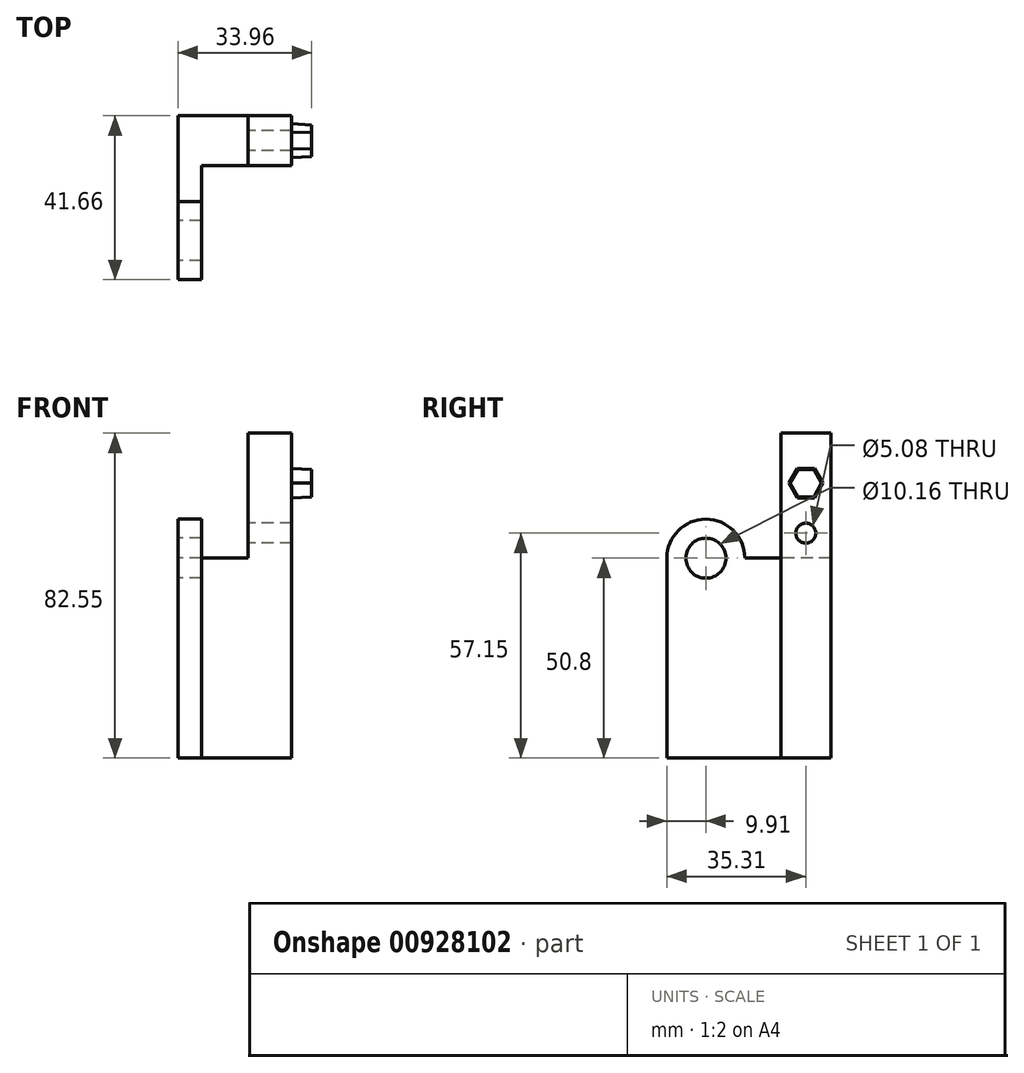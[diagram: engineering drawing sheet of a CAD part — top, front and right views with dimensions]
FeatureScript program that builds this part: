
annotation { "Feature Type Name" : "Feature", "Feature Type Description" : "" }
export const myFeature = defineFeature(function(context is Context, id is Id, definition is map)
    precondition{}
    {
        {
            var Q0;
            Q0=qCreatedBy(makeId("Right.planeOp"),FACE);
            var sketch = newSketch(context, id + "F0", { "sketchPlane" : qUnion([Q0])});
            skLineSegment(sketch, "E0.bottom", {"start": v(0, 50.8) * mm, "end": v(12.7, 50.8) * mm});
            skLineSegment(sketch, "E0.top", {"start": v(0, 0) * mm, "end": v(12.7, 0) * mm});
            skLineSegment(sketch, "E0.left", {"start": v(0, 50.8) * mm, "end": v(0, 0) * mm});
            skLineSegment(sketch, "E0.right", {"start": v(12.7, 50.8) * mm, "end": v(12.7, 0) * mm});
            skSolve(sketch);
        }
        {
            var Q0;
            Q0 = qSketchRegion(id + "F0", true);
            extrude(context, id + "F1", {"entities" : qUnion([Q0]), "depth" : 11.1 * mm, "offsetDistance" : 25.4 * mm});
        }
        {
            var Q0;
            Q0=makeQuery(id+"F1.opExtrude","CAP_FACE",FACE,{"disambiguationData":[OSD([sQuery(id+"F0.wireOp",EDGE,"E0.bottom"),sQuery(id+"F0.wireOp",EDGE,"E0.top"),sQuery(id+"F0.wireOp",EDGE,"E0.left"),sQuery(id+"F0.wireOp",EDGE,"E0.right")])],"isStart":false});
            var sketch = newSketch(context, id + "F2", { "sketchPlane" : qUnion([Q0])});
            skCircle(sketch, "E1.cCircle", {"center": v(6.35, 38.1) * mm, "radius": 3.74 * mm, "construction": true});
            skLineSegment(sketch, "E1.0", {"start": v(8.5, 34.36) * mm, "end": v(4.2, 34.36) * mm});
            skLineSegment(sketch, "E1.1", {"start": v(4.2, 34.36) * mm, "end": v(2.03, 38.1) * mm});
            skLineSegment(sketch, "E1.2", {"start": v(2.03, 38.1) * mm, "end": v(4.2, 41.84) * mm});
            skLineSegment(sketch, "E1.3", {"start": v(4.2, 41.84) * mm, "end": v(8.5, 41.84) * mm});
            skLineSegment(sketch, "E1.4", {"start": v(8.5, 41.84) * mm, "end": v(10.67, 38.1) * mm});
            skLineSegment(sketch, "E1.5", {"start": v(10.67, 38.1) * mm, "end": v(8.5, 34.36) * mm});
            skPoint(sketch, "E1.0.midPoint", {"position": v(6.35, 34.36) * mm});
            skLineSegment(sketch, "E2", {"start": v(6.35, 38.1) * mm, "end": v(6.35, 50.8) * mm, "construction": true});
            skSolve(sketch);
        }
        {
            var Q0;
            Q0 = qSketchRegion(id + "F2", true);
            extrude(context, id + "F3", {"entities" : qUnion([Q0]), "operationType" : NewBodyOperationType.ADD, "depth" : 5.08 * mm, "offsetDistance" : 25.4 * mm, "hasDraft" : true, "draftAngle" : 3 * degree, "draftPullDirection" : true});
        }
        {
            var Q0;
            Q0=makeQuery(id+"F1.opExtrude","CAP_FACE",FACE,{"disambiguationData":[OSD([sQuery(id+"F0.wireOp",EDGE,"E0.bottom"),sQuery(id+"F0.wireOp",EDGE,"E0.top"),sQuery(id+"F0.wireOp",EDGE,"E0.left"),sQuery(id+"F0.wireOp",EDGE,"E0.right")])],"isStart":true});
            var sketch = newSketch(context, id + "F4", { "sketchPlane" : qUnion([Q0])});
            skCircle(sketch, "E3", {"center": v(-6.35, 25.4) * mm, "radius": 2.54 * mm});
            skPoint(sketch, "E3.centerSnap0", {"position": v(-6.35, 50.8) * mm});
            skSolve(sketch);
        }
        {
            var Q0;
            Q0 = qSketchRegion(id + "F4", true);
            extrude(context, id + "F5", {"entities" : qUnion([Q0]), "operationType" : NewBodyOperationType.REMOVE, "endBound" : BoundingType.THROUGH_ALL, "oppositeDirection" : true, "depth" : 25.4 * mm, "offsetDistance" : 25.4 * mm});
        }
        {
            var Q0;
            Q0=makeQuery(id+"F1.opExtrude","CAP_FACE",FACE,{"disambiguationData":[OSD([sQuery(id+"F0.wireOp",EDGE,"E0.bottom"),sQuery(id+"F0.wireOp",EDGE,"E0.top"),sQuery(id+"F0.wireOp",EDGE,"E0.left"),sQuery(id+"F0.wireOp",EDGE,"E0.right")])],"isStart":true});
            var sketch = newSketch(context, id + "F6", { "sketchPlane" : qUnion([Q0])});
            skLineSegment(sketch, "E4.bottom", {"start": v(-12.7, 0) * mm, "end": v(0, 0) * mm});
            skLineSegment(sketch, "E4.top", {"start": v(-12.7, 19.05) * mm, "end": v(0, 19.05) * mm});
            skLineSegment(sketch, "E4.left", {"start": v(-12.7, 0) * mm, "end": v(-12.7, 19.05) * mm});
            skLineSegment(sketch, "E4.right", {"start": v(0, 0) * mm, "end": v(0, 19.05) * mm});
            skSolve(sketch);
        }
        {
            var Q0;
            Q0 = qSketchRegion(id + "F6", true);
            extrude(context, id + "F7", {"entities" : qUnion([Q0]), "operationType" : NewBodyOperationType.ADD, "depth" : 17.78 * mm, "offsetDistance" : 25.4 * mm});
        }
        {
            var Q0;
            Q0=makeQuery(id+"F7.boolean.opBoolean","MERGE",FACE,{"derivedFrom":[makeQuery(id+"F1.opExtrude","SWEPT_FACE",FACE,{"disambiguationData":[OSD([sQuery(id+"F0.wireOp",EDGE,"E0.left")])]}),makeQuery(id+"F7.opExtrude","SWEPT_FACE",FACE,{"disambiguationData":[OSD([sQuery(id+"F6.wireOp",EDGE,"E4.right")])]})]});
            var sketch = newSketch(context, id + "F8", { "sketchPlane" : qUnion([Q0])});
            skLineSegment(sketch, "E5.bottom", {"start": v(-17.78, 0) * mm, "end": v(-11.84, 0) * mm});
            skLineSegment(sketch, "E5.top", {"start": v(-17.78, 19.05) * mm, "end": v(-11.84, 19.05) * mm});
            skLineSegment(sketch, "E5.left", {"start": v(-17.78, 0) * mm, "end": v(-17.78, 19.05) * mm});
            skLineSegment(sketch, "E5.right", {"start": v(-11.84, 0) * mm, "end": v(-11.84, 19.05) * mm});
            skSolve(sketch);
        }
        {
            var Q0;
            Q0 = qSketchRegion(id + "F8", true);
            extrude(context, id + "F9", {"entities" : qUnion([Q0]), "operationType" : NewBodyOperationType.ADD, "depth" : 25.4 * mm, "offsetDistance" : 25.4 * mm});
        }
        {
            var Q0;
            Q0=makeQuery(id+"F9.boolean.opBoolean","MERGE",FACE,{"derivedFrom":[makeQuery(id+"F7.opExtrude","SWEPT_FACE",FACE,{"disambiguationData":[OSD([sQuery(id+"F6.wireOp",EDGE,"E4.top")])]}),makeQuery(id+"F9.opExtrude","SWEPT_FACE",FACE,{"disambiguationData":[OSD([sQuery(id+"F8.wireOp",EDGE,"E5.top")])]})]});
            var sketch = newSketch(context, id + "F10", { "sketchPlane" : qUnion([Q0])});
            skLineSegment(sketch, "E6.bottom", {"start": v(-17.78, -25.4) * mm, "end": v(-11.84, -25.4) * mm});
            skLineSegment(sketch, "E6.top", {"start": v(-17.78, -12.7) * mm, "end": v(-11.84, -12.7) * mm});
            skLineSegment(sketch, "E6.left", {"start": v(-17.78, -25.4) * mm, "end": v(-17.78, -12.7) * mm});
            skLineSegment(sketch, "E6.right", {"start": v(-11.84, -25.4) * mm, "end": v(-11.84, -12.7) * mm});
            skSolve(sketch);
        }
        {
            var Q0;
            Q0 = qSketchRegion(id + "F10", true);
            extrude(context, id + "F11", {"entities" : qUnion([Q0]), "operationType" : NewBodyOperationType.ADD, "depth" : 6.35 * mm, "offsetDistance" : 25.4 * mm});
        }
        {
            var Q0;
            Q0=makeQuery(id+"F11.opExtrude","CAP_EDGE",EDGE,{"disambiguationData":[OSD([sQuery(id+"F10.wireOp",EDGE,"E6.top")])],"isStart":false});
            var Q1;
            Q1=makeQuery(id+"F11.opExtrude","CAP_EDGE",EDGE,{"disambiguationData":[OSD([sQuery(id+"F10.wireOp",EDGE,"E6.bottom")])],"isStart":false});
            fillet(context, id + "F12", {"entities" : qUnion([Q0, Q1]), "radius" : 6.35 * mm, "tangentPropagation" : true, "allowEdgeOverflow" : false});
        }
        {
            var Q0;
            Q0=makeQuery(id+"F11.boolean.opBoolean","MERGE",FACE,{"derivedFrom":[makeQuery(id+"F9.boolean.opBoolean","MERGE",FACE,{"derivedFrom":[makeQuery(id+"F7.opExtrude","CAP_FACE",FACE,{"disambiguationData":[OSD([sQuery(id+"F6.wireOp",EDGE,"E4.bottom"),sQuery(id+"F6.wireOp",EDGE,"E4.top"),sQuery(id+"F6.wireOp",EDGE,"E4.left"),sQuery(id+"F6.wireOp",EDGE,"E4.right")])],"isStart":false}),makeQuery(id+"F9.opExtrude","SWEPT_FACE",FACE,{"disambiguationData":[OSD([sQuery(id+"F8.wireOp",EDGE,"E5.left")])]})]}),makeQuery(id+"F11.opExtrude","SWEPT_FACE",FACE,{"disambiguationData":[OSD([sQuery(id+"F10.wireOp",EDGE,"E6.left")])]})]});
            var sketch = newSketch(context, id + "F13", { "sketchPlane" : qUnion([Q0])});
            skCircle(sketch, "E7", {"center": v(19.05, 19.05) * mm, "radius": 5.08 * mm});
            skSolve(sketch);
        }
        {
            var Q0;
            Q0 = qSketchRegion(id + "F13", true);
            extrude(context, id + "F14", {"entities" : qUnion([Q0]), "operationType" : NewBodyOperationType.REMOVE, "endBound" : BoundingType.THROUGH_ALL, "oppositeDirection" : true, "depth" : 25.4 * mm, "offsetDistance" : 25.4 * mm});
        }
        {
            var Q0;
            Q0=makeQuery(id+"F11.boolean.opBoolean","MERGE",FACE,{"derivedFrom":[makeQuery(id+"F9.boolean.opBoolean","MERGE",FACE,{"derivedFrom":[makeQuery(id+"F7.opExtrude","CAP_FACE",FACE,{"disambiguationData":[OSD([sQuery(id+"F6.wireOp",EDGE,"E4.bottom"),sQuery(id+"F6.wireOp",EDGE,"E4.top"),sQuery(id+"F6.wireOp",EDGE,"E4.left"),sQuery(id+"F6.wireOp",EDGE,"E4.right")])],"isStart":false}),makeQuery(id+"F9.opExtrude","SWEPT_FACE",FACE,{"disambiguationData":[OSD([sQuery(id+"F8.wireOp",EDGE,"E5.left")])]})]}),makeQuery(id+"F11.opExtrude","SWEPT_FACE",FACE,{"disambiguationData":[OSD([sQuery(id+"F10.wireOp",EDGE,"E6.left")])]})]});
            var sketch = newSketch(context, id + "F15", { "sketchPlane" : qUnion([Q0])});
            skArc(sketch, "E8", {"start": v(28.96, 19.05) * mm, "mid": v(19.05, 28.96) * mm, "end": v(9.14, 19.05) * mm});
            skLineSegment(sketch, "E9", {"start": v(28.96, 19.05) * mm, "end": v(28.96, 0) * mm});
            skLineSegment(sketch, "E10", {"start": v(28.96, 0) * mm, "end": v(25.4, 0) * mm});
            skLineSegment(sketch, "E11", {"start": v(25.4, 0) * mm, "end": v(25.4, 19.05) * mm});
            skArc(sketch, "E12", {"start": v(25.4, 19.05) * mm, "mid": v(19.05, 25.4) * mm, "end": v(12.7, 19.05) * mm});
            skLineSegment(sketch, "E13", {"start": v(12.7, 19.05) * mm, "end": v(9.14, 19.05) * mm});
            skSolve(sketch);
        }
        {
            var Q0;
            Q0 = qSketchRegion(id + "F15", true);
            var Q1;
            Q1=makeQuery(id+"F11.boolean.opBoolean","MERGE",FACE,{"derivedFrom":[makeQuery(id+"F9.opExtrude","SWEPT_FACE",FACE,{"disambiguationData":[OSD([sQuery(id+"F8.wireOp",EDGE,"E5.right")])]}),makeQuery(id+"F11.opExtrude","SWEPT_FACE",FACE,{"disambiguationData":[OSD([sQuery(id+"F10.wireOp",EDGE,"E6.right")])]})]});
            extrude(context, id + "F16", {"entities" : qUnion([Q0]), "operationType" : NewBodyOperationType.ADD, "endBound" : BoundingType.UP_TO_SURFACE, "oppositeDirection" : true, "depth" : 25.4 * mm, "endBoundEntityFace" : qUnion([Q1]), "offsetDistance" : 25.4 * mm});
        }
        {
            var Q0;
            Q0=makeQuery(id+"F16.boolean.opBoolean","MERGE",FACE,{"derivedFrom":[makeQuery(id+"F9.boolean.opBoolean","MERGE",FACE,{"derivedFrom":[makeQuery(id+"F7.boolean.opBoolean","MERGE",FACE,{"derivedFrom":[makeQuery(id+"F1.opExtrude","SWEPT_FACE",FACE,{"disambiguationData":[OSD([sQuery(id+"F0.wireOp",EDGE,"E0.top")])]}),makeQuery(id+"F7.opExtrude","SWEPT_FACE",FACE,{"disambiguationData":[OSD([sQuery(id+"F6.wireOp",EDGE,"E4.bottom")])]})]}),makeQuery(id+"F9.opExtrude","SWEPT_FACE",FACE,{"disambiguationData":[OSD([sQuery(id+"F8.wireOp",EDGE,"E5.bottom")])]})]}),makeQuery(id+"F16.opExtrude","SWEPT_FACE",FACE,{"disambiguationData":[OSD([sQuery(id+"F15.wireOp",EDGE,"E10")])]})]});
            var sketch = newSketch(context, id + "F17", { "sketchPlane" : qUnion([Q0])});
            skLineSegment(sketch, "E14", {"start": v(11.1, -12.7) * mm, "end": v(-17.78, -12.7) * mm});
            skLineSegment(sketch, "E15", {"start": v(-17.78, -12.7) * mm, "end": v(-17.78, 28.96) * mm});
            skLineSegment(sketch, "E16", {"start": v(-17.78, 28.96) * mm, "end": v(-11.84, 28.96) * mm});
            skLineSegment(sketch, "E17", {"start": v(-11.84, 28.96) * mm, "end": v(-11.84, 0) * mm});
            skLineSegment(sketch, "E18", {"start": v(-11.84, 0) * mm, "end": v(11.1, 0) * mm});
            skLineSegment(sketch, "E19", {"start": v(11.1, 0) * mm, "end": v(11.1, -12.7) * mm});
            skSolve(sketch);
        }
        {
            var Q0;
            Q0 = qSketchRegion(id + "F17", true);
            extrude(context, id + "F18", {"entities" : qUnion([Q0]), "operationType" : NewBodyOperationType.ADD, "depth" : 31.75 * mm, "offsetDistance" : 25.4 * mm});
        }
    });
